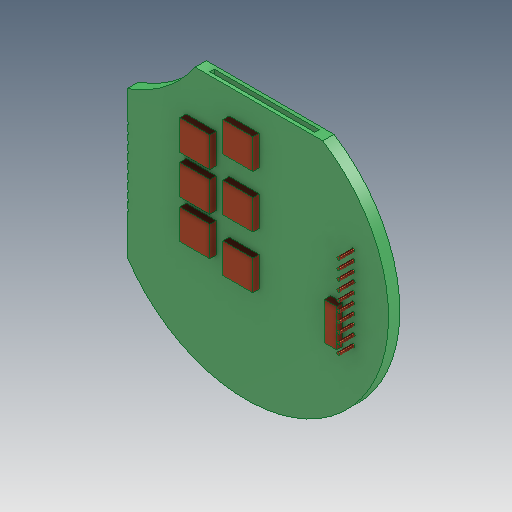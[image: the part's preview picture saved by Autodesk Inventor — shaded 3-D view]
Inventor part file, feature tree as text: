
AUTODESK INVENTOR PART (.ipt)
format: ipt  version: 2020.3 (Build 243373010, 373A)  size: 261,120 bytes
history: native  units: mm
features: sketch x6, extrude x6, plane x1, pattern_linear x1, projected_geometry x1
ambient origin geometry x8: Origin, YZ Plane, XZ Plane, XY Plane, X Axis, Y Axis, Z Axis, Center Point
bodies: Solid1 (feature_tree)
feature tree (15):
  sketch  "Sketch1"  dims[d0=4.0mm d1=4.0mm d2=4.0mm d3=4.0mm d4=4.0mm d5=4.0mm d6=4.0mm d7=4.0mm d8=4.0mm d9=4.0mm d10=6.0mm d11=4.0mm d12=1.15mm d13=1.15mm d14=4.0mm d15=4.0mm d16=1.75mm d17=2.65mm d18=3.0mm d19=3.0mm d20=5.0mm d21=1.65mm d22=11.25mm d25=1.5mm d26=0.0mm]
  extrude  "Extrusion2"  Depth=1.5mm TaperAngle=0.0deg
  extrude  "Extrusion3"  Depth=1.5mm
  sketch  "Sketch4"  dims[d36=18.5mm d37=16.0mm]
  extrude  "Extrusion5"  Depth=18.5mm
  extrude  "Extrusion6"  Depth=1.5mm
  plane  "Work Plane1"
  sketch  "Sketch9"  dims[d43=14.0mm d44=2.5mm d45=0.0mm d46=0.75mm d47=0.85mm d48=0.0mm d49=2.0mm d50=0.0mm d51=100.0mm d53=11.0mm]
  extrude  "Extrusion7"  Depth=0.45mm
  extrude  "Extrusion8"  Depth=2.5mm TaperAngle=0.0deg
  pattern_linear  "Rectangular Pattern2"  Spacing1=0.75mm  [1 undecoded]
  sketch  "Sketch3"  dims[d28=1.5mm d29=0.0mm d30=15.85mm]
  sketch  "Sketch5"  dims[d38=10.0mm d39=0.0mm d40=1.5mm]
  sketch  "Sketch6"  dims[d41=0.45mm d42=0.45mm]
  projected_geometry  "Projected Loop1"
note: 1 required parameter value undecoded (feature->parameter linkage not recoverable at this tier; creation-order binding heuristic only, values carry confidence <= 0.55)
